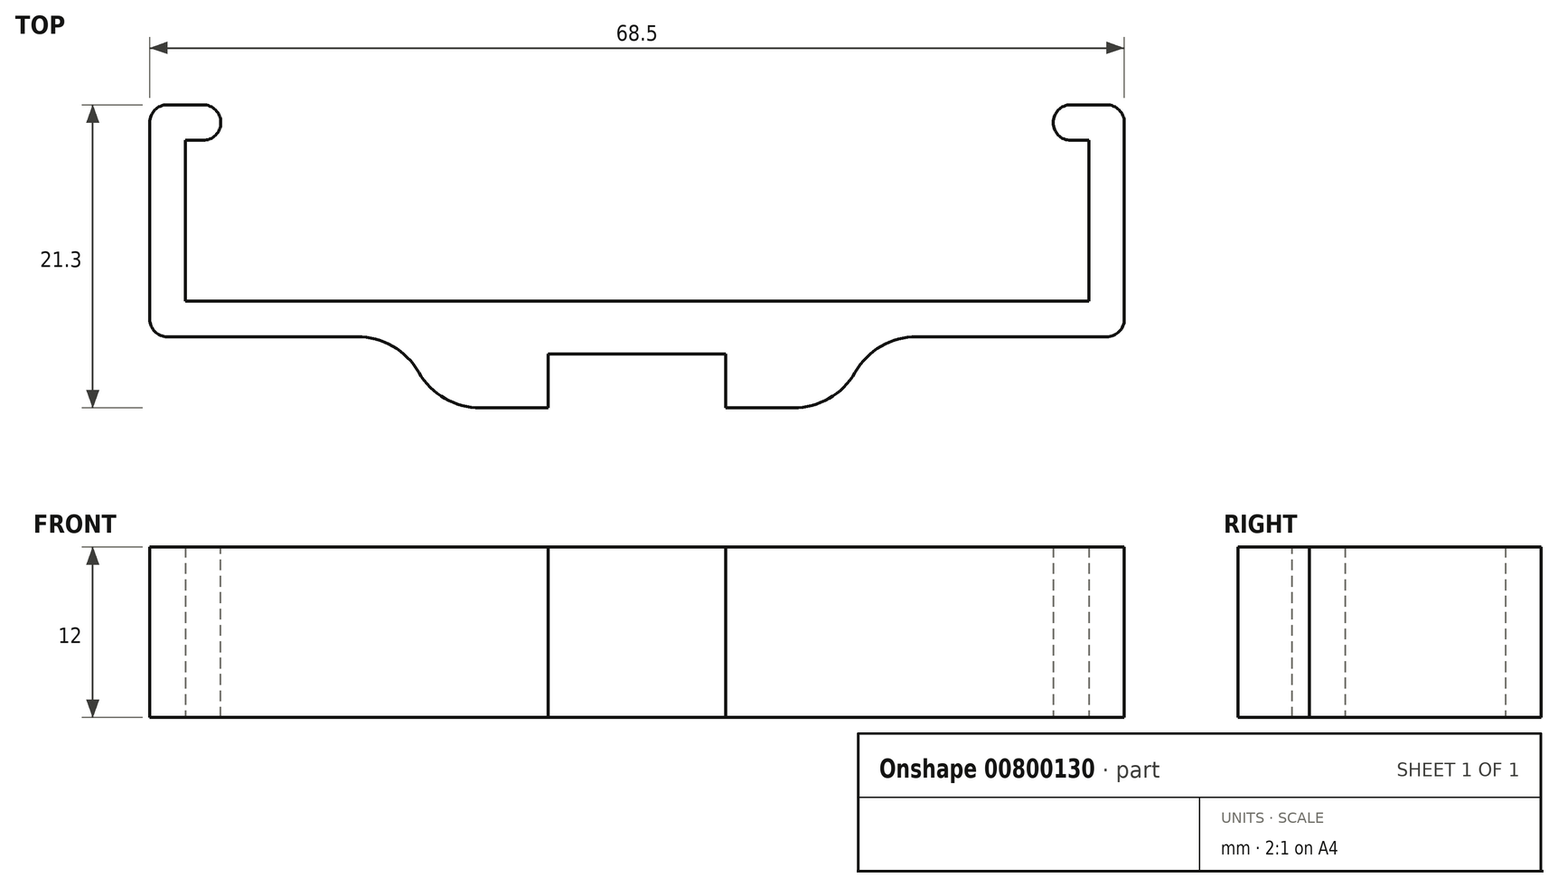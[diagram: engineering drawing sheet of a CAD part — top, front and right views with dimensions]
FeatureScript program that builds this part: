
annotation { "Feature Type Name" : "Feature", "Feature Type Description" : "" }
export const myFeature = defineFeature(function(context is Context, id is Id, definition is map)
    precondition{}
    {
        {
            var Q0;
            Q0=qCreatedBy(makeId("Top.planeOp"),FACE);
            var sketch = newSketch(context, id + "F0", { "sketchPlane" : qUnion([Q0])});
            skLineSegment(sketch, "E0.bottom", {"start": v(31.75, 1.25) * mm, "end": v(-31.75, 1.25) * mm});
            skLineSegment(sketch, "E0.top", {"start": v(31.75, -1.25) * mm, "end": v(-31.75, -1.25) * mm});
            skLineSegment(sketch, "E0.left", {"start": v(31.75, 1.25) * mm, "end": v(31.75, -1.25) * mm});
            skLineSegment(sketch, "E0.right", {"start": v(-31.75, 1.25) * mm, "end": v(-31.75, -1.25) * mm});
            skPoint(sketch, "E0.middle", {"position": v(0, 0) * mm});
            skLineSegment(sketch, "E1.bottom", {"start": v(11, -6.25) * mm, "end": v(-11, -6.25) * mm});
            skLineSegment(sketch, "E1.top", {"start": v(11, -1.25) * mm, "end": v(-11, -1.25) * mm});
            skLineSegment(sketch, "E1.left", {"start": v(11, -6.25) * mm, "end": v(11, -1.25) * mm});
            skLineSegment(sketch, "E1.right", {"start": v(-11, -6.25) * mm, "end": v(-11, -1.25) * mm});
            skPoint(sketch, "E1.middle", {"position": v(0, -3.75) * mm});
            skArc(sketch, "E2", {"start": v(-11, -6.25) * mm, "mid": v(-14.54, -4.79) * mm, "end": v(-16, -1.25) * mm});
            skLineSegment(sketch, "E3.bottom", {"start": v(-31.75, -1.25) * mm, "end": v(-34.25, -1.25) * mm});
            skLineSegment(sketch, "E3.top", {"start": v(-31.75, 12.55) * mm, "end": v(-34.25, 12.55) * mm});
            skLineSegment(sketch, "E3.left", {"start": v(-31.75, -1.25) * mm, "end": v(-31.75, 12.55) * mm});
            skLineSegment(sketch, "E3.right", {"start": v(-34.25, -1.25) * mm, "end": v(-34.25, 12.55) * mm});
            skLineSegment(sketch, "E4.MirrorCS", {"start": v(31.75, 12.55) * mm, "end": v(34.25, 12.55) * mm});
            skLineSegment(sketch, "E5.MirrorCS", {"start": v(34.25, -1.25) * mm, "end": v(34.25, 12.55) * mm});
            skLineSegment(sketch, "E6.MirrorCS", {"start": v(31.75, -1.25) * mm, "end": v(31.75, 12.55) * mm});
            skLineSegment(sketch, "E7.MirrorCS", {"start": v(31.75, -1.25) * mm, "end": v(34.25, -1.25) * mm});
            skArc(sketch, "E8.MirrorCS", {"start": v(11, -6.25) * mm, "mid": v(14.54, -4.79) * mm, "end": v(16, -1.25) * mm});
            skLineSegment(sketch, "E9.bottom", {"start": v(-34.25, 12.55) * mm, "end": v(-29.25, 12.55) * mm});
            skLineSegment(sketch, "E9.top", {"start": v(-34.25, 15.05) * mm, "end": v(-29.25, 15.05) * mm});
            skLineSegment(sketch, "E9.left", {"start": v(-34.25, 12.55) * mm, "end": v(-34.25, 15.05) * mm});
            skLineSegment(sketch, "E9.right", {"start": v(-29.25, 12.55) * mm, "end": v(-29.25, 15.05) * mm});
            skLineSegment(sketch, "E10.MirrorCS", {"start": v(34.25, 15.05) * mm, "end": v(29.25, 15.05) * mm});
            skLineSegment(sketch, "E11.MirrorCS", {"start": v(34.25, 12.55) * mm, "end": v(34.25, 15.05) * mm});
            skLineSegment(sketch, "E12.MirrorCS", {"start": v(34.25, 12.55) * mm, "end": v(29.25, 12.55) * mm});
            skLineSegment(sketch, "E13.MirrorCS", {"start": v(29.25, 12.55) * mm, "end": v(29.25, 15.05) * mm});
            skSolve(sketch);
        }
        {
            var Q0;
            Q0 = qSketchRegion(id + "F0", true);
            extrude(context, id + "F1", {"entities" : qUnion([Q0]), "depth" : 12 * mm, "offsetDistance" : 25 * mm});
        }
        {
            var Q0;
            Q0=makeQuery(id+"F1.opExtrude","CAP_FACE",FACE,{"disambiguationData":[OSD([sQuery(id+"F0.wireOp",EDGE,"E0.bottom"),sQuery(id+"F0.wireOp",EDGE,"E0.top"),sQuery(id+"F0.wireOp",EDGE,"E1.bottom"),sQuery(id+"F0.wireOp",EDGE,"E2"),sQuery(id+"F0.wireOp",EDGE,"E3.bottom"),sQuery(id+"F0.wireOp",EDGE,"E3.top"),sQuery(id+"F0.wireOp",EDGE,"E3.left"),sQuery(id+"F0.wireOp",EDGE,"E3.right"),sQuery(id+"F0.wireOp",EDGE,"E4.MirrorCS"),sQuery(id+"F0.wireOp",EDGE,"E5.MirrorCS"),sQuery(id+"F0.wireOp",EDGE,"E6.MirrorCS"),sQuery(id+"F0.wireOp",EDGE,"E7.MirrorCS"),sQuery(id+"F0.wireOp",EDGE,"E8.MirrorCS")])],"isStart":false});
            var sketch = newSketch(context, id + "F2", { "sketchPlane" : qUnion([Q0])});
            skLineSegment(sketch, "E14.bottom", {"start": v(6.25, -6.25) * mm, "end": v(-6.25, -6.25) * mm});
            skLineSegment(sketch, "E14.top", {"start": v(6.25, -2.45) * mm, "end": v(-6.25, -2.45) * mm});
            skLineSegment(sketch, "E14.left", {"start": v(6.25, -6.25) * mm, "end": v(6.25, -2.45) * mm});
            skLineSegment(sketch, "E14.right", {"start": v(-6.25, -6.25) * mm, "end": v(-6.25, -2.45) * mm});
            skPoint(sketch, "E14.middle", {"position": v(0, -4.35) * mm});
            skSolve(sketch);
        }
        {
            var Q0;
            Q0 = qSketchRegion(id + "F2", true);
            extrude(context, id + "F3", {"entities" : qUnion([Q0]), "operationType" : NewBodyOperationType.REMOVE, "endBound" : BoundingType.UP_TO_NEXT, "oppositeDirection" : true, "depth" : 25 * mm, "offsetDistance" : 25 * mm});
        }
        {
            var Q0;
            Q0=makeQuery(id+"F1.opExtrude","SWEPT_EDGE",EDGE,{"disambiguationData":[OSD([sQuery(id+"F0.wireOp",EDGE,"E0.top"),sQuery(id+"F0.wireOp",EDGE,"E8.MirrorCS")])]});
            var Q1;
            Q1=makeQuery(id+"F1.opExtrude","SWEPT_EDGE",EDGE,{"disambiguationData":[OSD([sQuery(id+"F0.wireOp",EDGE,"E0.top"),sQuery(id+"F0.wireOp",EDGE,"E2")])]});
            fillet(context, id + "F4", {"entities" : qUnion([Q0, Q1]), "radius" : 5 * mm, "tangentPropagation" : true, "allowEdgeOverflow" : false});
        }
        {
            var Q0;
            Q0=makeQuery(id+"F1.opExtrude","SWEPT_EDGE",EDGE,{"disambiguationData":[OSD([sQuery(id+"F0.wireOp",EDGE,"E3.bottom"),sQuery(id+"F0.wireOp",EDGE,"E3.right")])]});
            var Q1;
            Q1=makeQuery(id+"F1.opExtrude","SWEPT_EDGE",EDGE,{"disambiguationData":[OSD([sQuery(id+"F0.wireOp",EDGE,"E5.MirrorCS"),sQuery(id+"F0.wireOp",EDGE,"E7.MirrorCS")])]});
            var Q2;
            Q2=makeQuery(id+"F1.opExtrude","SWEPT_EDGE",EDGE,{"disambiguationData":[OSD([sQuery(id+"F0.wireOp",EDGE,"E9.top"),sQuery(id+"F0.wireOp",EDGE,"E9.left")])]});
            var Q3;
            Q3=makeQuery(id+"F1.opExtrude","SWEPT_EDGE",EDGE,{"disambiguationData":[OSD([sQuery(id+"F0.wireOp",EDGE,"E9.top"),sQuery(id+"F0.wireOp",EDGE,"E9.right")])]});
            var Q4;
            Q4=makeQuery(id+"F1.opExtrude","SWEPT_EDGE",EDGE,{"disambiguationData":[OSD([sQuery(id+"F0.wireOp",EDGE,"E9.bottom"),sQuery(id+"F0.wireOp",EDGE,"E9.right")])]});
            var Q5;
            Q5=makeQuery(id+"F1.opExtrude","SWEPT_EDGE",EDGE,{"disambiguationData":[OSD([sQuery(id+"F0.wireOp",EDGE,"E12.MirrorCS"),sQuery(id+"F0.wireOp",EDGE,"E13.MirrorCS")])]});
            var Q6;
            Q6=makeQuery(id+"F1.opExtrude","SWEPT_EDGE",EDGE,{"disambiguationData":[OSD([sQuery(id+"F0.wireOp",EDGE,"E10.MirrorCS"),sQuery(id+"F0.wireOp",EDGE,"E13.MirrorCS")])]});
            var Q7;
            Q7=makeQuery(id+"F1.opExtrude","SWEPT_EDGE",EDGE,{"disambiguationData":[OSD([sQuery(id+"F0.wireOp",EDGE,"E10.MirrorCS"),sQuery(id+"F0.wireOp",EDGE,"E11.MirrorCS")])]});
            fillet(context, id + "F5", {"entities" : qUnion([Q0, Q1, Q2, Q3, Q4, Q5, Q6, Q7]), "radius" : 1.25 * mm, "tangentPropagation" : true, "allowEdgeOverflow" : false});
        }
    });
